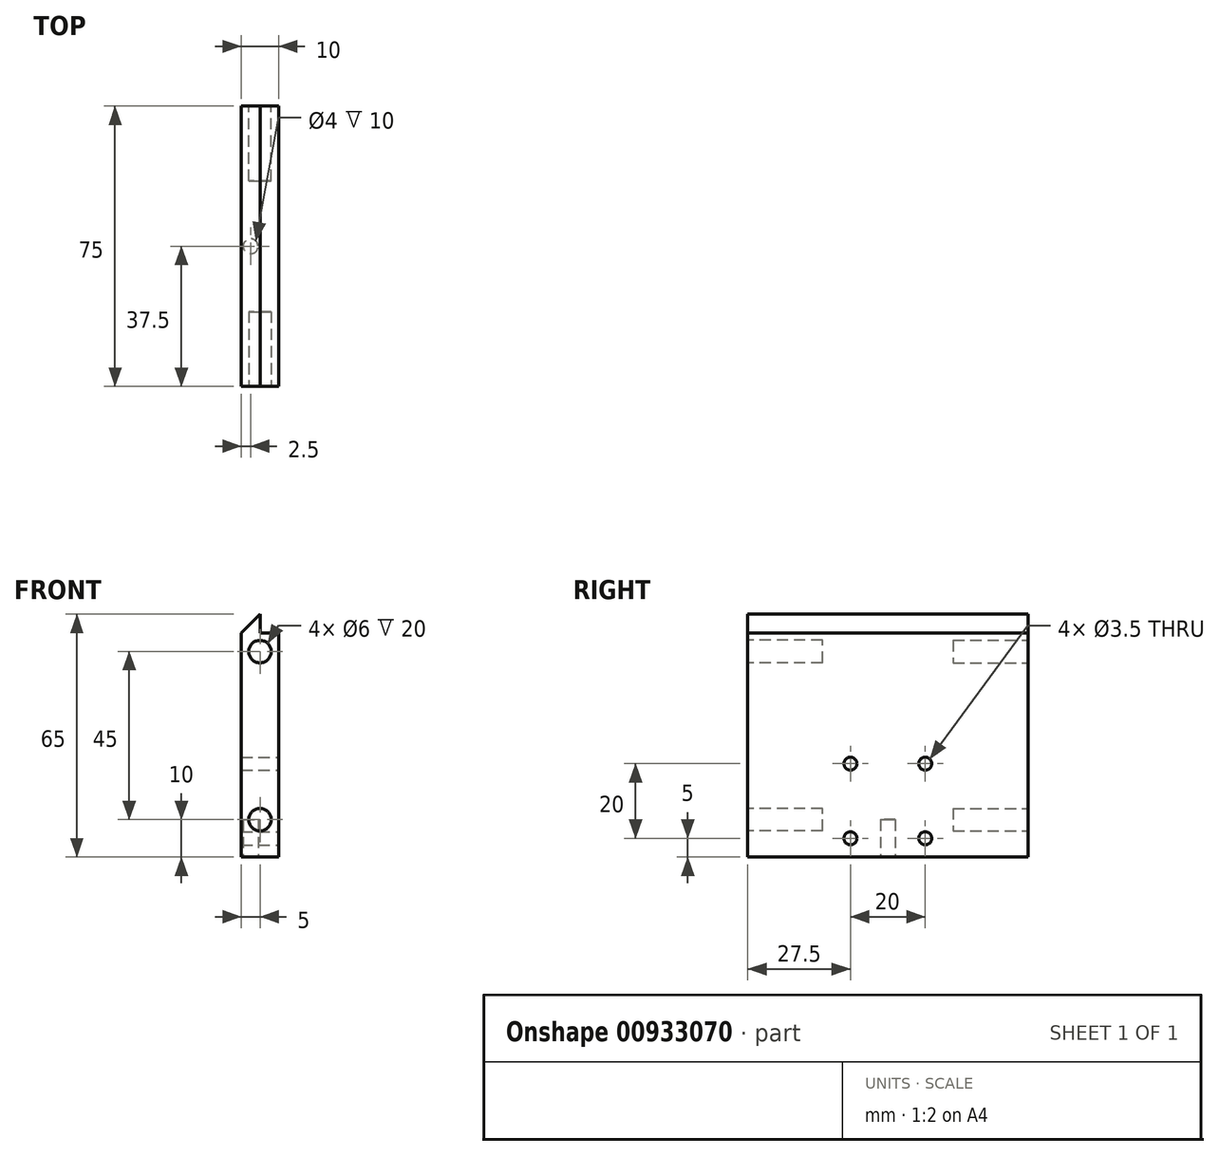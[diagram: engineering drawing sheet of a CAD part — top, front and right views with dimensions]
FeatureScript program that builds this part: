
annotation { "Feature Type Name" : "Feature", "Feature Type Description" : "" }
export const myFeature = defineFeature(function(context is Context, id is Id, definition is map)
    precondition{}
    {
        {
            var Q0;
            Q0=qCreatedBy(makeId("Front.planeOp"),FACE);
            var sketch = newSketch(context, id + "F0", { "sketchPlane" : qUnion([Q0])});
            skLineSegment(sketch, "E0.top", {"start": v(-5, -32.5) * mm, "end": v(5, -32.5) * mm});
            skLineSegment(sketch, "E0.left", {"start": v(-5, 27.5) * mm, "end": v(-5, -32.5) * mm});
            skLineSegment(sketch, "E0.right", {"start": v(5, 27.5) * mm, "end": v(5, -32.5) * mm});
            skPoint(sketch, "E0.middle", {"position": v(0, 0) * mm});
            skPoint(sketch, "E1", {"position": v(0, -22.5) * mm});
            skPoint(sketch, "E2", {"position": v(0, 22.5) * mm});
            skLineSegment(sketch, "E3", {"start": v(0, 32.5) * mm, "end": v(-5, 27.5) * mm});
            skLineSegment(sketch, "E4.top", {"start": v(0, 27.5) * mm, "end": v(5, 27.5) * mm});
            skLineSegment(sketch, "E4.left", {"start": v(0, 32.5) * mm, "end": v(0, 27.5) * mm});
            skSolve(sketch);
        }
        {
            var Q0;
            {var subQ1=sQuery(id+"F0.wireOp",EDGE,"E0.top");Q0=makeQuery(id+"F0.imprint","IMPRINT",FACE,{"disambiguationData":[TD([[makeQuery(id+"F0.imprint","IMPRINT",EDGE,{"derivedFrom":subQ1}),1.0]])]});}
            extrude(context, id + "F1", {"entities" : qUnion([Q0]), "depth" : 75 * mm, "offsetDistance" : 25 * mm});
        }
        {
            var Q0;
            Q0=makeQuery(id+"F1.opExtrude","SWEPT_FACE",FACE,{"disambiguationData":[OSD([sQuery(id+"F0.wireOp",EDGE,"E0.top")])]});
            var sketch = newSketch(context, id + "F2", { "sketchPlane" : qUnion([Q0])});
            skPoint(sketch, "E5.centerSnap0", {"position": v(-5, 37.5) * mm});
            skCircle(sketch, "E6", {"center": v(-2.5, 37.5) * mm, "radius": 2 * mm});
            skSolve(sketch);
        }
        {
            var Q0;
            Q0=makeQuery(id+"F1.opExtrude","SWEPT_FACE",FACE,{"disambiguationData":[OSD([sQuery(id+"F0.wireOp",EDGE,"E0.right")])]});
            var sketch = newSketch(context, id + "F3", { "sketchPlane" : qUnion([Q0])});
            skCircle(sketch, "E7", {"center": v(-27.5, -7.5) * mm, "radius": 1.75 * mm});
            skCircle(sketch, "E8", {"center": v(-47.5, -7.5) * mm, "radius": 1.75 * mm});
            skCircle(sketch, "E9", {"center": v(-27.5, -27.5) * mm, "radius": 1.75 * mm});
            skCircle(sketch, "E10", {"center": v(-47.5, -27.5) * mm, "radius": 1.75 * mm});
            skSolve(sketch);
        }
        {
            var Q0;
            Q0=qSketchRegion(id+"F3",true);
            extrude(context, id + "F4", {"entities" : qUnion([Q0]), "operationType" : NewBodyOperationType.REMOVE, "oppositeDirection" : true, "depth" : 25 * mm, "offsetDistance" : 25 * mm});
        }
        {
            var Q0;
            Q0=makeQuery(id+"F1.opExtrude","SWEPT_FACE",FACE,{"disambiguationData":[OSD([sQuery(id+"F0.wireOp",EDGE,"E0.top")])]});
            var sketch = newSketch(context, id + "F5", { "sketchPlane" : qUnion([Q0])});
            skSolve(sketch);
        }
        {
            var Q0;
            Q0=makeQuery(id+"F1.opExtrude","CAP_FACE",FACE,{"disambiguationData":[OSD([sQuery(id+"F0.wireOp",EDGE,"E0.top"),sQuery(id+"F0.wireOp",EDGE,"E0.left"),sQuery(id+"F0.wireOp",EDGE,"E0.right"),sQuery(id+"F0.wireOp",EDGE,"E3"),sQuery(id+"F0.wireOp",EDGE,"E4.top"),sQuery(id+"F0.wireOp",EDGE,"E4.left")])],"isStart":false});
            var sketch = newSketch(context, id + "F6", { "sketchPlane" : qUnion([Q0])});
            skCircle(sketch, "E11", {"center": v(0, -22.5) * mm, "radius": 3 * mm});
            skPoint(sketch, "E11.centerSnap0", {"position": v(0, -32.5) * mm});
            skSolve(sketch);
        }
        {
            var Q0;
            Q0=qSketchRegion(id+"F6",true);
            extrude(context, id + "F7", {"entities" : qUnion([Q0]), "operationType" : NewBodyOperationType.REMOVE, "oppositeDirection" : true, "depth" : 20 * mm, "offsetDistance" : 25 * mm});
        }
        {
            var Q0;
            Q0=makeQuery(id+"F1.opExtrude","CAP_FACE",FACE,{"disambiguationData":[OSD([sQuery(id+"F0.wireOp",EDGE,"E0.top"),sQuery(id+"F0.wireOp",EDGE,"E0.left"),sQuery(id+"F0.wireOp",EDGE,"E0.right"),sQuery(id+"F0.wireOp",EDGE,"E3"),sQuery(id+"F0.wireOp",EDGE,"E4.top"),sQuery(id+"F0.wireOp",EDGE,"E4.left")])],"isStart":false});
            var sketch = newSketch(context, id + "F8", { "sketchPlane" : qUnion([Q0])});
            skCircle(sketch, "E12", {"center": v(0, 22.5) * mm, "radius": 3 * mm});
            skSolve(sketch);
        }
        {
            var Q0;
            Q0=qSketchRegion(id+"F8",true);
            extrude(context, id + "F9", {"entities" : qUnion([Q0]), "operationType" : NewBodyOperationType.REMOVE, "oppositeDirection" : true, "depth" : 20 * mm, "offsetDistance" : 25 * mm});
        }
        {
            var Q0;
            Q0=makeQuery(id+"F1.opExtrude","CAP_FACE",FACE,{"disambiguationData":[OSD([sQuery(id+"F0.wireOp",EDGE,"E0.top"),sQuery(id+"F0.wireOp",EDGE,"E0.left"),sQuery(id+"F0.wireOp",EDGE,"E0.right"),sQuery(id+"F0.wireOp",EDGE,"E3"),sQuery(id+"F0.wireOp",EDGE,"E4.top"),sQuery(id+"F0.wireOp",EDGE,"E4.left")])],"isStart":true});
            var sketch = newSketch(context, id + "F10", { "sketchPlane" : qUnion([Q0])});
            skCircle(sketch, "E13", {"center": v(0, -22.5) * mm, "radius": 3 * mm});
            skPoint(sketch, "E13.centerSnap0", {"position": v(0, -32.5) * mm});
            skSolve(sketch);
        }
        {
            var Q0;
            Q0=qSketchRegion(id+"F10",true);
            extrude(context, id + "F11", {"entities" : qUnion([Q0]), "operationType" : NewBodyOperationType.REMOVE, "oppositeDirection" : true, "depth" : 20 * mm, "offsetDistance" : 25 * mm});
        }
        {
            var Q0;
            Q0=makeQuery(id+"F1.opExtrude","CAP_FACE",FACE,{"disambiguationData":[OSD([sQuery(id+"F0.wireOp",EDGE,"E0.top"),sQuery(id+"F0.wireOp",EDGE,"E0.left"),sQuery(id+"F0.wireOp",EDGE,"E0.right"),sQuery(id+"F0.wireOp",EDGE,"E3"),sQuery(id+"F0.wireOp",EDGE,"E4.top"),sQuery(id+"F0.wireOp",EDGE,"E4.left")])],"isStart":true});
            var sketch = newSketch(context, id + "F12", { "sketchPlane" : qUnion([Q0])});
            skCircle(sketch, "E14", {"center": v(0, 22.5) * mm, "radius": 3 * mm});
            skPoint(sketch, "E14.centerSnap0", {"position": v(0, -32.5) * mm});
            skSolve(sketch);
        }
        {
            var Q0;
            Q0=qSketchRegion(id+"F12",true);
            extrude(context, id + "F13", {"entities" : qUnion([Q0]), "operationType" : NewBodyOperationType.REMOVE, "oppositeDirection" : true, "depth" : 20 * mm, "offsetDistance" : 25 * mm});
        }
        {
            var Q0;
            Q0=qSketchRegion(id+"F2",true);
            extrude(context, id + "F14", {"entities" : qUnion([Q0]), "operationType" : NewBodyOperationType.REMOVE, "oppositeDirection" : true, "depth" : 10 * mm, "offsetDistance" : 25 * mm});
        }
        {
            var Q0;
            Q0=qSketchRegion(id+"F3",true);
            extrude(context, id + "F15", {"entities" : qUnion([Q0]), "operationType" : NewBodyOperationType.REMOVE, "oppositeDirection" : true, "depth" : 25 * mm, "offsetDistance" : 25 * mm});
        }
        {
            var Q0;
            Q0=qSketchRegion(id+"F3",true);
            extrude(context, id + "F16", {"entities" : qUnion([Q0]), "operationType" : NewBodyOperationType.REMOVE, "oppositeDirection" : true, "depth" : 25 * mm, "offsetDistance" : 25 * mm});
        }
        {
            var Q0;
            Q0=qSketchRegion(id+"F3",true);
            extrude(context, id + "F17", {"entities" : qUnion([Q0]), "operationType" : NewBodyOperationType.REMOVE, "oppositeDirection" : true, "depth" : 25 * mm, "offsetDistance" : 25 * mm});
        }
    });
